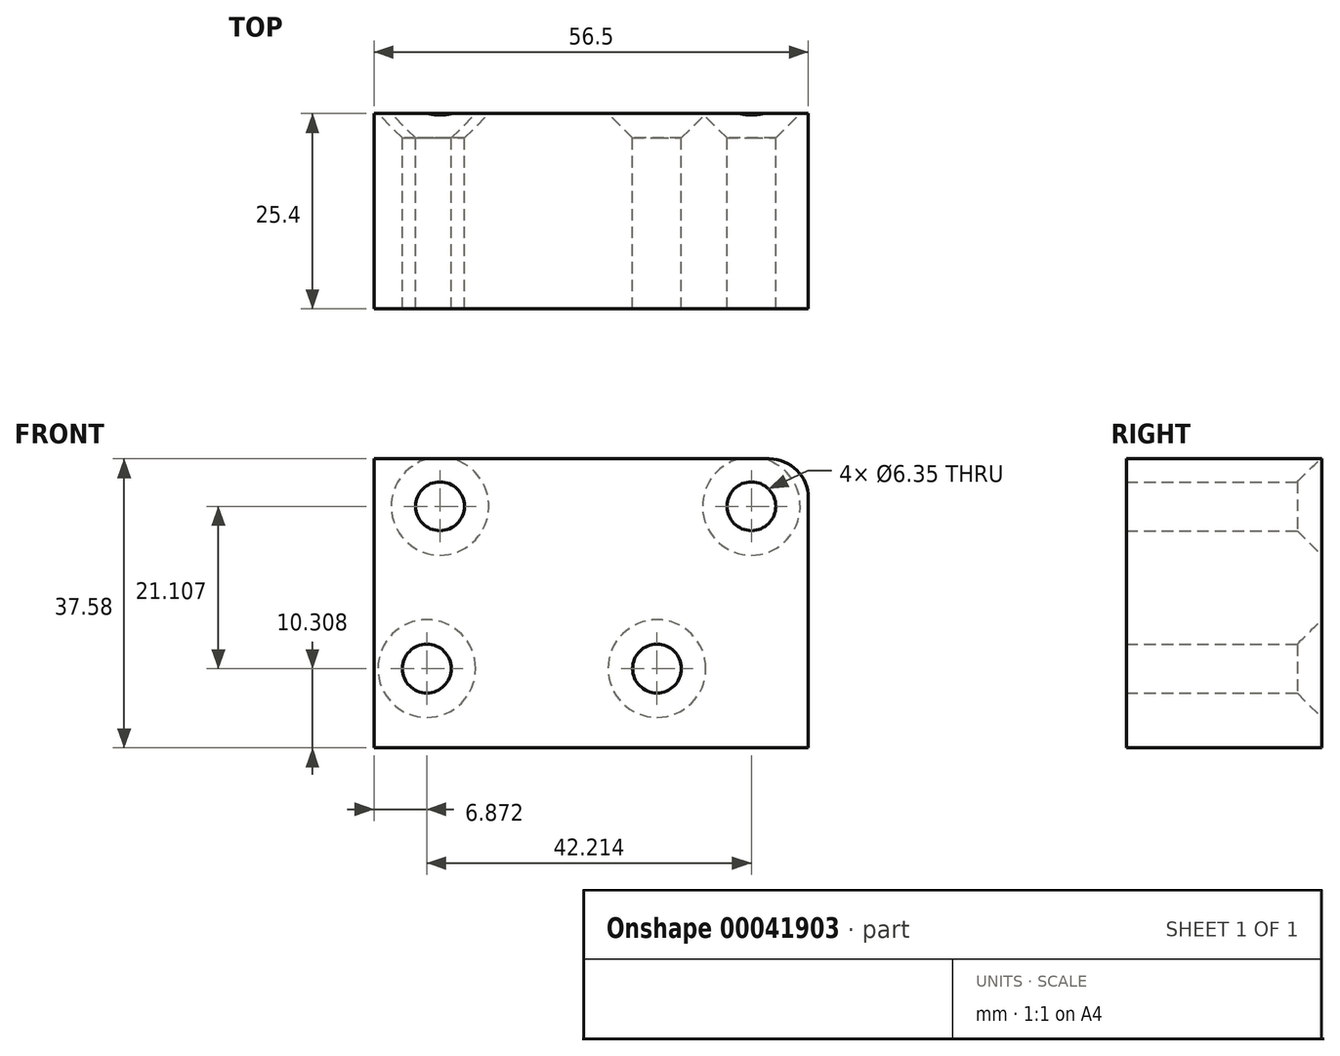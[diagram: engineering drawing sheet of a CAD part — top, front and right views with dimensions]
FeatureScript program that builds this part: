
annotation { "Feature Type Name" : "Feature", "Feature Type Description" : "" }
export const myFeature = defineFeature(function(context is Context, id is Id, definition is map)
    precondition{}
    {
        {
            var Q0;
            Q0=qCreatedBy(makeId("Front.planeOp"),FACE);
            var sketch = newSketch(context, id + "F0", { "sketchPlane" : qUnion([Q0])});
            skLineSegment(sketch, "E0.bottom", {"start": v(0, 0) * mm, "end": v(56.5, 0) * mm});
            skLineSegment(sketch, "E0.top", {"start": v(0, 37.58) * mm, "end": v(56.5, 37.58) * mm});
            skLineSegment(sketch, "E0.left", {"start": v(0, 0) * mm, "end": v(0, 37.58) * mm});
            skLineSegment(sketch, "E0.right", {"start": v(56.5, 0) * mm, "end": v(56.5, 37.58) * mm});
            skSolve(sketch);
        }
        {
            var Q0;
            Q0 = qSketchRegion(id + "F0", true);
            extrude(context, id + "F1", {"entities" : qUnion([Q0]), "depth" : 25.4 * mm});
        }
        {
            var Q0;
            Q0=makeQuery(id+"F1.opExtrude","SWEPT_EDGE",EDGE,{"disambiguationData":[OSD([sQuery(id+"F0.wireOp",EDGE,"E0.top"),sQuery(id+"F0.wireOp",EDGE,"E0.right")])]});
            fillet(context, id + "F2", {"entities" : qUnion([Q0]), "radius" : 5.08 * mm, "tangentPropagation" : true, "allowEdgeOverflow" : false});
        }
        {
            var Q0;
            Q0=qCreatedBy(makeId("Front.planeOp"),FACE);
            var sketch = newSketch(context, id + "F3", { "sketchPlane" : qUnion([Q0])});
            skPoint(sketch, "E1", {"position": v(8.6, 31.41) * mm});
            skPoint(sketch, "E2", {"position": v(49.09, 31.41) * mm});
            skPoint(sketch, "E3", {"position": v(36.81, 10.3) * mm});
            skPoint(sketch, "E4", {"position": v(6.87, 10.3) * mm});
            skSolve(sketch);
        }
        {
            var Q0;
            Q0=sQuery(id+"F3.wireOp",VERTEX,"E1");
            var Q1;
            Q1=sQuery(id+"F3.wireOp",VERTEX,"E4");
            var Q2;
            Q2=sQuery(id+"F3.wireOp",VERTEX,"E3");
            var Q3;
            Q3=sQuery(id+"F3.wireOp",VERTEX,"E2");
            var Q4;
            Q4=makeQuery(id+"F1.opExtrude","SWEPT_BODY",BODY,{"disambiguationData":[OSD([sQuery(id+"F0.wireOp",EDGE,"E0.bottom"),sQuery(id+"F0.wireOp",EDGE,"E0.top"),sQuery(id+"F0.wireOp",EDGE,"E0.left"),sQuery(id+"F0.wireOp",EDGE,"E0.right")])]});
            hole(context, id + "F4", {"style" : HoleStyle.C_SINK, "holeDiameter" : 6.35 * mm, "cSinkDiameter" : 12.7 * mm, "endStyle" : HoleEndStyle.THROUGH, "oppositeDirection" : true, "locations" : qUnion([Q0, Q1, Q2, Q3]), "scope" : qUnion([Q4]), "cSinkAngle" : 90 * degree});
        }
    });
